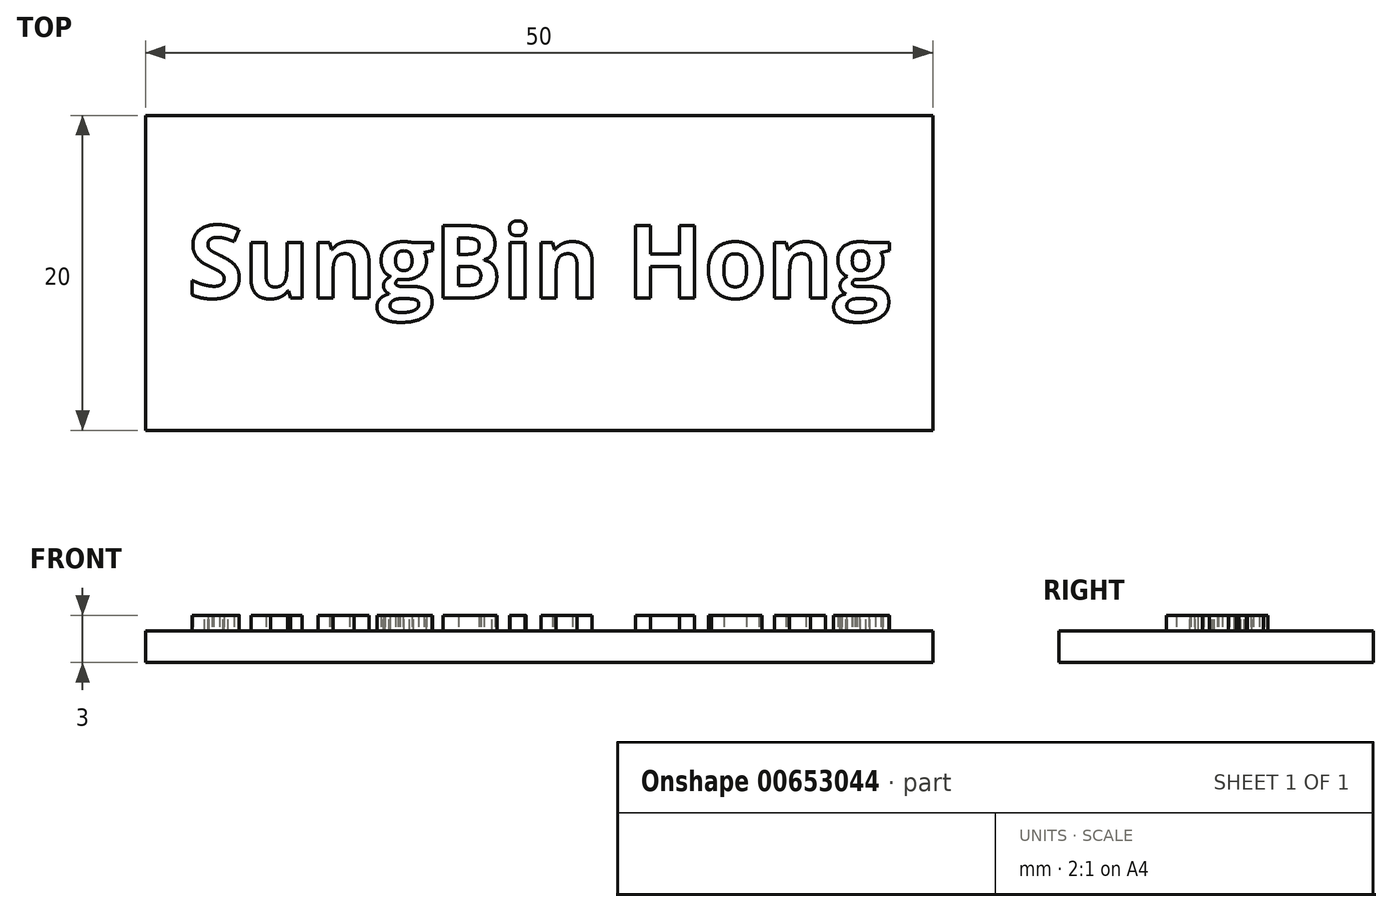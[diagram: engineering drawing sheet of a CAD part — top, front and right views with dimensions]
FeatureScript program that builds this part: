
annotation { "Feature Type Name" : "Feature", "Feature Type Description" : "" }
export const myFeature = defineFeature(function(context is Context, id is Id, definition is map)
    precondition{}
    {
        {
            var Q0;
            Q0=qCreatedBy(makeId("Top.planeOp"),FACE);
            var sketch = newSketch(context, id + "F0", { "sketchPlane" : qUnion([Q0])});
            skLineSegment(sketch, "E0.bottom", {"start": v(0, 0) * mm, "end": v(50, 0) * mm});
            skLineSegment(sketch, "E0.top", {"start": v(0, 20) * mm, "end": v(50, 20) * mm});
            skLineSegment(sketch, "E0.left", {"start": v(0, 0) * mm, "end": v(0, 20) * mm});
            skLineSegment(sketch, "E0.right", {"start": v(50, 0) * mm, "end": v(50, 20) * mm});
            skSolve(sketch);
        }
        {
            var Q0;
            Q0=makeQuery(id+"F0.imprint","IMPRINT",FACE,{"disambiguationData":[TD([[makeQuery(id+"F0.imprint","IMPRINT",EDGE,{"derivedFrom":sQuery(id+"F0.wireOp",EDGE,"E0.bottom")}),1.0]])]});
            extrude(context, id + "F1", {"entities" : qUnion([Q0]), "depth" : 2 * mm, "offsetDistance" : 25.4 * mm});
        }
        {
            var Q0;
            Q0=makeQuery(id+"F1.opExtrude","CAP_FACE",FACE,{"disambiguationData":[OSD([sQuery(id+"F0.wireOp",EDGE,"E0.bottom"),sQuery(id+"F0.wireOp",EDGE,"E0.top"),sQuery(id+"F0.wireOp",EDGE,"E0.left"),sQuery(id+"F0.wireOp",EDGE,"E0.right")])],"isStart":false});
            var sketch = newSketch(context, id + "F2", { "sketchPlane" : qUnion([Q0])});
            skText(sketch, "E1", { "text": "SungBin Hong", "fontName": "OpenSans-Bold.ttf"});
            const initialGuessF2  = {"E1": [0.00266, 0.0084, 1, 0, 0.00464]};
            skSetInitialGuess(sketch, initialGuessF2);
            skSolve(sketch);
        }
        {
            var Q0;
            Q0 = qSketchRegion(id + "F2", true);
            extrude(context, id + "F3", {"entities" : qUnion([Q0]), "operationType" : NewBodyOperationType.ADD, "depth" : 1 * mm, "offsetDistance" : 25.4 * mm});
        }
    });
